# Revit family: montigo-residential-single-sided-fireplace-DELRAY-DRL6013
name_source: partatom
category: Generic Models
units: mm (PartAtom-declared; Revit-internal decimal feet)

## family parameters
Always vertical = Yes
Can host rebar = No
Cut with Voids When Loaded = No
Part Type = Normal
Room Calculation Point = No
Round Connector Dimension = Use Diameter
Shared = No
Work Plane-Based = No

## types (1)
- montigo-residential-single-sided-fireplace-DELRAY-DRL6013
    Base Height = 6 5/8"
    Description = Montigo Fireplace as Specified
    Fire Place - Opening = 16 5/8"
    Fire Place Height = 24 1/2"
    Fire Place Length = 62 1/2"
    Firebox Material = Metal - Montigo - White
    Frame Material = Metal - Montigo - Black
    Glazing Tint = Glass - Montigo - Tint as Specified
    Length = 65 1/2"
    Manufacturer = Montigo
    Manufacturer Website = https://www.montigo.com
    URL = https://www.montigo.com
    Width = 12 3/8"

## geometry (parser evidence)
native form markers: Sweep x5
no freeform markers — native parametric forms only
